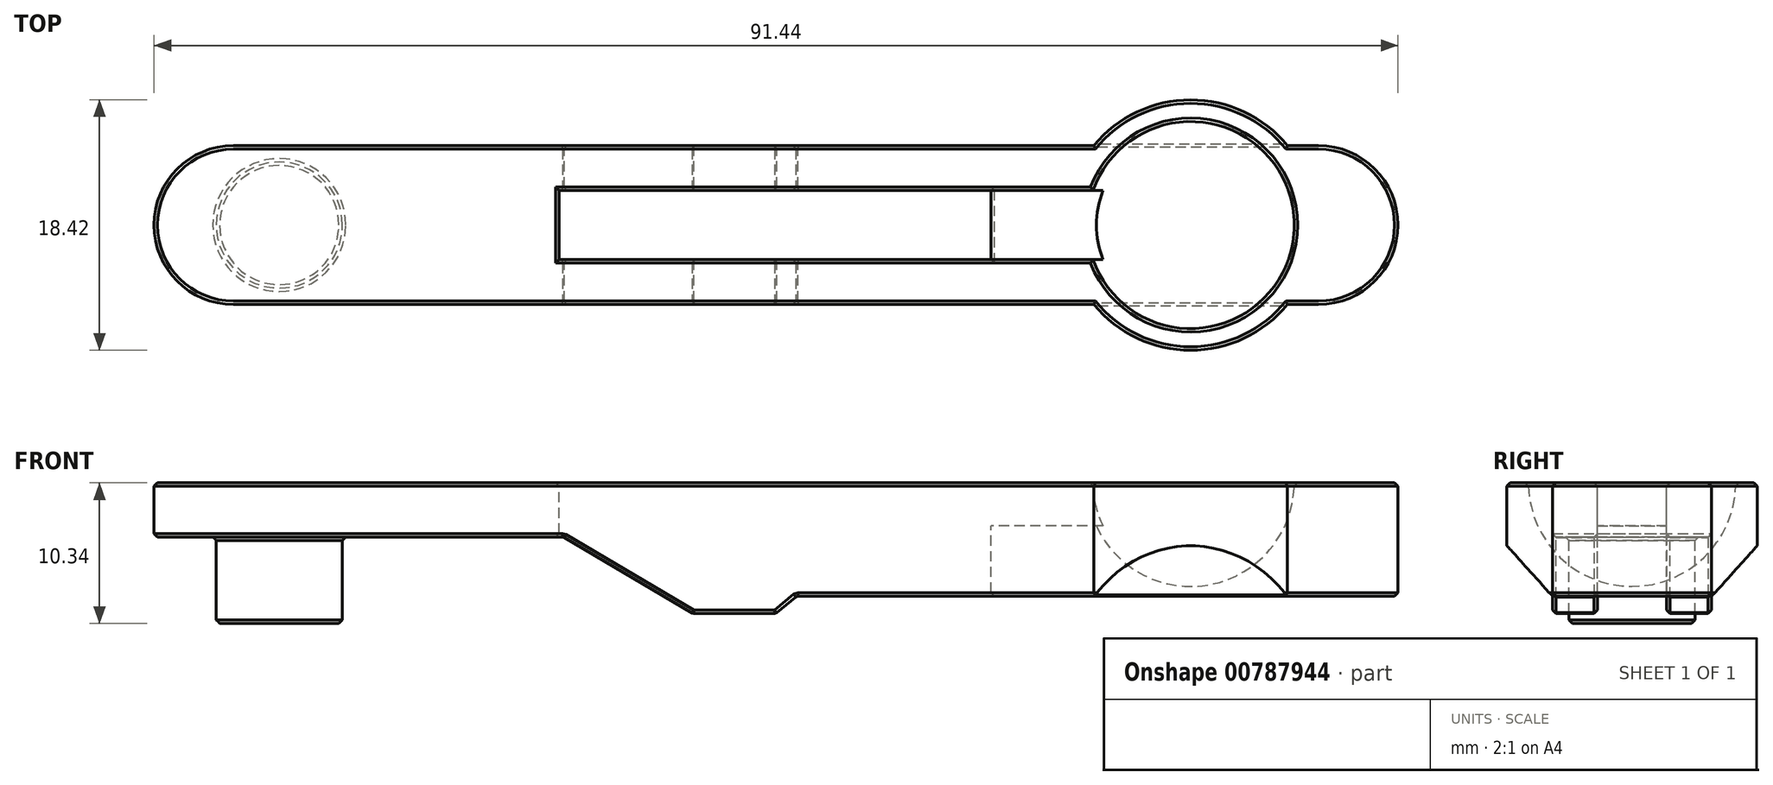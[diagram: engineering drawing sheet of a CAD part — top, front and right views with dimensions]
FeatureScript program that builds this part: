
annotation { "Feature Type Name" : "Feature", "Feature Type Description" : "" }
export const myFeature = defineFeature(function(context is Context, id is Id, definition is map)
    precondition{}
    {
        {
            var Q0;
            Q0=qCreatedBy(makeId("Top.planeOp"),FACE);
            var sketch = newSketch(context, id + "F0", { "sketchPlane" : qUnion([Q0])});
            skLineSegment(sketch, "E0.bottom", {"start": v(45.72, 5.84) * mm, "end": v(-45.72, 5.84) * mm});
            skLineSegment(sketch, "E0.top", {"start": v(45.72, -5.84) * mm, "end": v(-45.72, -5.84) * mm});
            skLineSegment(sketch, "E0.left", {"start": v(45.72, 5.84) * mm, "end": v(45.72, -5.84) * mm});
            skLineSegment(sketch, "E0.right", {"start": v(-45.72, 5.84) * mm, "end": v(-45.72, -5.84) * mm});
            skPoint(sketch, "E0.middle", {"position": v(0, 0) * mm});
            skSolve(sketch);
        }
        {
            var Q0;
            Q0 = qSketchRegion(id + "F0", true);
            extrude(context, id + "F1", {"entities" : qUnion([Q0]), "depth" : 9.6 * mm, "offsetDistance" : 25.4 * mm});
        }
        {
            var Q0;
            Q0=makeQuery(id+"F1.opExtrude","SWEPT_EDGE",EDGE,{"disambiguationData":[OSD([sQuery(id+"F0.wireOp",EDGE,"E0.top"),sQuery(id+"F0.wireOp",EDGE,"E0.right")])]});
            var Q1;
            Q1=makeQuery(id+"F1.opExtrude","SWEPT_EDGE",EDGE,{"disambiguationData":[OSD([sQuery(id+"F0.wireOp",EDGE,"E0.bottom"),sQuery(id+"F0.wireOp",EDGE,"E0.right")])]});
            var Q2;
            Q2=makeQuery(id+"F1.opExtrude","SWEPT_EDGE",EDGE,{"disambiguationData":[OSD([sQuery(id+"F0.wireOp",EDGE,"E0.top"),sQuery(id+"F0.wireOp",EDGE,"E0.left")])]});
            var Q3;
            Q3=makeQuery(id+"F1.opExtrude","SWEPT_EDGE",EDGE,{"disambiguationData":[OSD([sQuery(id+"F0.wireOp",EDGE,"E0.bottom"),sQuery(id+"F0.wireOp",EDGE,"E0.left")])]});
            fillet(context, id + "F2", {"entities" : qUnion([Q0, Q1, Q2, Q3]), "tangentPropagation" : true, "radius" : 5.84 * mm, "defaultsChanged" : true, "vertexSettings" : [], "allowEdgeOverflow" : false});
        }
        {
            var Q0;
            Q0=makeQuery(id+"F1.opExtrude","CAP_FACE",FACE,{"disambiguationData":[OSD([sQuery(id+"F0.wireOp",EDGE,"E0.bottom"),sQuery(id+"F0.wireOp",EDGE,"E0.top"),sQuery(id+"F0.wireOp",EDGE,"E0.left"),sQuery(id+"F0.wireOp",EDGE,"E0.right")])],"isStart":false});
            var sketch = newSketch(context, id + "F3", { "sketchPlane" : qUnion([Q0])});
            skCircle(sketch, "E1", {"center": v(30.48, 0) * mm, "radius": 9.2 * mm});
            skSolve(sketch);
        }
        {
            var Q0;
            Q0 = qSketchRegion(id + "F3", true);
            var Q1;
            Q1=makeQuery(id+"F1.opExtrude","CAP_FACE",FACE,{"disambiguationData":[OSD([sQuery(id+"F0.wireOp",EDGE,"E0.bottom"),sQuery(id+"F0.wireOp",EDGE,"E0.top"),sQuery(id+"F0.wireOp",EDGE,"E0.left"),sQuery(id+"F0.wireOp",EDGE,"E0.right")])],"isStart":true});
            extrude(context, id + "F4", {"entities" : qUnion([Q0]), "operationType" : NewBodyOperationType.ADD, "endBound" : BoundingType.UP_TO_SURFACE, "oppositeDirection" : true, "depth" : 25.4 * mm, "endBoundEntityFace" : qUnion([Q1]), "offsetDistance" : 25.4 * mm});
        }
        {
            var Q0;
            Q0=makeQuery(id+"F4.boolean.opBoolean","MERGE",FACE,{"derivedFrom":[makeQuery(id+"F1.opExtrude","CAP_FACE",FACE,{"disambiguationData":[OSD([sQuery(id+"F0.wireOp",EDGE,"E0.bottom"),sQuery(id+"F0.wireOp",EDGE,"E0.top"),sQuery(id+"F0.wireOp",EDGE,"E0.left"),sQuery(id+"F0.wireOp",EDGE,"E0.right")])],"isStart":false}),makeQuery(id+"F4.opExtrude","CAP_FACE",FACE,{"disambiguationData":[OSD([sQuery(id+"F3.wireOp",EDGE,"E1")])],"isStart":true})]});
            var sketch = newSketch(context, id + "F5", { "sketchPlane" : qUnion([Q0])});
            skArc(sketch, "E2", {"start": v(38.1, 0) * mm, "mid": v(30.48, 7.62) * mm, "end": v(22.86, 0) * mm});
            skLineSegment(sketch, "E3", {"start": v(22.86, 0) * mm, "end": v(38.1, 0) * mm});
            skLineSegment(sketch, "E4", {"start": v(13.82, 0) * mm, "end": v(42.87, 0) * mm, "construction": true});
            skSolve(sketch);
        }
        {
            var Q0;
            Q0 = qSketchRegion(id + "F5", true);
            var Q1;
            Q1=sQuery(id+"F5.wireOp",EDGE,"E4");
            revolve(context, id + "F6", {"operationType" : NewBodyOperationType.REMOVE, "surfaceOperationType" : NewSurfaceOperationType.NEW, "entities" : qUnion([Q0]), "axis" : qUnion([Q1]), "revolveType" : RevolveType.FULL});
        }
        {
            var Q0;
            Q0=makeQuery(id+"F4.boolean.opBoolean","MERGE",FACE,{"derivedFrom":[makeQuery(id+"F1.opExtrude","CAP_FACE",FACE,{"disambiguationData":[OSD([sQuery(id+"F0.wireOp",EDGE,"E0.bottom"),sQuery(id+"F0.wireOp",EDGE,"E0.top"),sQuery(id+"F0.wireOp",EDGE,"E0.left"),sQuery(id+"F0.wireOp",EDGE,"E0.right")])],"isStart":false}),makeQuery(id+"F4.opExtrude","CAP_FACE",FACE,{"disambiguationData":[OSD([sQuery(id+"F3.wireOp",EDGE,"E1")])],"isStart":true})]});
            var sketch = newSketch(context, id + "F7", { "sketchPlane" : qUnion([Q0])});
            skLineSegment(sketch, "E5.bottom", {"start": v(15.8, 2.54) * mm, "end": v(-15.95, 2.54) * mm});
            skLineSegment(sketch, "E5.top", {"start": v(15.8, -2.54) * mm, "end": v(-15.95, -2.54) * mm});
            skLineSegment(sketch, "E5.left", {"start": v(15.8, 2.54) * mm, "end": v(15.8, -2.54) * mm});
            skLineSegment(sketch, "E5.right", {"start": v(-15.95, 2.54) * mm, "end": v(-15.95, -2.54) * mm});
            skPoint(sketch, "E5.middle", {"position": v(-0.08, 0) * mm});
            skSolve(sketch);
        }
        {
            var Q0;
            Q0 = qSketchRegion(id + "F7", true);
            extrude(context, id + "F8", {"entities" : qUnion([Q0]), "operationType" : NewBodyOperationType.REMOVE, "endBound" : BoundingType.THROUGH_ALL, "oppositeDirection" : true, "depth" : 25.4 * mm, "offsetDistance" : 25.4 * mm});
        }
        {
            var Q0;
            Q0=makeQuery(id+"F4.boolean.opBoolean","MERGE",FACE,{"derivedFrom":[makeQuery(id+"F1.opExtrude","CAP_FACE",FACE,{"disambiguationData":[OSD([sQuery(id+"F0.wireOp",EDGE,"E0.bottom"),sQuery(id+"F0.wireOp",EDGE,"E0.top"),sQuery(id+"F0.wireOp",EDGE,"E0.left"),sQuery(id+"F0.wireOp",EDGE,"E0.right")])],"isStart":false}),makeQuery(id+"F4.opExtrude","CAP_FACE",FACE,{"disambiguationData":[OSD([sQuery(id+"F3.wireOp",EDGE,"E1")])],"isStart":true})]});
            var sketch = newSketch(context, id + "F9", { "sketchPlane" : qUnion([Q0])});
            skLineSegment(sketch, "E6.bottom", {"start": v(12.7, -2.54) * mm, "end": v(25.4, -2.54) * mm});
            skLineSegment(sketch, "E6.top", {"start": v(12.7, 2.54) * mm, "end": v(25.4, 2.54) * mm});
            skLineSegment(sketch, "E6.left", {"start": v(12.7, -2.54) * mm, "end": v(12.7, 2.54) * mm});
            skLineSegment(sketch, "E6.right", {"start": v(25.4, -2.54) * mm, "end": v(25.4, 2.54) * mm});
            skSolve(sketch);
        }
        {
            var Q0;
            Q0 = qSketchRegion(id + "F9", true);
            extrude(context, id + "F10", {"entities" : qUnion([Q0]), "operationType" : NewBodyOperationType.REMOVE, "oppositeDirection" : true, "depth" : 3.17 * mm, "offsetDistance" : 25.4 * mm});
        }
        {
            var Q0;
            Q0=qCreatedBy(makeId("Front.planeOp"),FACE);
            var sketch = newSketch(context, id + "F11", { "sketchPlane" : qUnion([Q0])});
            skLineSegment(sketch, "E7", {"start": v(0, 0) * mm, "end": v(1.52, 1.27) * mm});
            skLineSegment(sketch, "E8", {"start": v(1.52, 1.27) * mm, "end": v(46.53, 1.27) * mm});
            skLineSegment(sketch, "E9", {"start": v(46.53, 1.27) * mm, "end": v(46.53, 0) * mm});
            skLineSegment(sketch, "E10", {"start": v(46.53, 0) * mm, "end": v(0, 0) * mm});
            skLineSegment(sketch, "E11", {"start": v(-6.1, 0) * mm, "end": v(-15.62, 5.61) * mm});
            skLineSegment(sketch, "E12", {"start": v(-15.62, 5.61) * mm, "end": v(-45.72, 5.61) * mm});
            skLineSegment(sketch, "E13", {"start": v(-45.72, 5.61) * mm, "end": v(-45.72, 0) * mm});
            skLineSegment(sketch, "E14", {"start": v(-45.72, 0) * mm, "end": v(-6.1, 0) * mm});
            skSolve(sketch);
        }
        {
            var Q0;
            Q0 = qSketchRegion(id + "F11", true);
            extrude(context, id + "F12", {"entities" : qUnion([Q0]), "operationType" : NewBodyOperationType.REMOVE, "depth" : 19.05 * mm, "offsetDistance" : 25.4 * mm, "hasSecondDirection" : true, "secondDirectionBound" : BoundingType.THROUGH_ALL, "secondDirectionOppositeDirection" : true, "secondDirectionDepth" : 25.4 * mm, "symmetric" : true});
        }
        {
            var Q0;
            Q0=makeQuery(id+"F12.boolean.opBoolean","COPY",FACE,{"derivedFrom":makeQuery(id+"F12.opExtrude","SWEPT_FACE",FACE,{"disambiguationData":[OSD([sQuery(id+"F11.wireOp",EDGE,"E12")])]})});
            var sketch = newSketch(context, id + "F13", { "sketchPlane" : qUnion([Q0])});
            skCircle(sketch, "E15", {"center": v(-36.51, 0) * mm, "radius": 4.64 * mm});
            skSolve(sketch);
        }
        {
            var Q0;
            Q0 = qSketchRegion(id + "F13", true);
            extrude(context, id + "F14", {"entities" : qUnion([Q0]), "operationType" : NewBodyOperationType.ADD, "depth" : 6.35 * mm, "offsetDistance" : 25.4 * mm});
        }
        {
            var Q0;
            Q0=qCreatedBy(makeId("Right.planeOp"),FACE);
            var sketch = newSketch(context, id + "F15", { "sketchPlane" : qUnion([Q0])});
            skLineSegment(sketch, "E16", {"start": v(5.84, 1.24) * mm, "end": v(9.27, 5.05) * mm});
            skLineSegment(sketch, "E17", {"start": v(9.27, 5.05) * mm, "end": v(9.27, 1.24) * mm});
            skLineSegment(sketch, "E18", {"start": v(9.27, 1.24) * mm, "end": v(5.84, 1.24) * mm});
            skLineSegment(sketch, "E19.MirrorCS", {"start": v(-9.27, 1.24) * mm, "end": v(-5.84, 1.24) * mm});
            skLineSegment(sketch, "E20.MirrorCS", {"start": v(-9.27, 5.05) * mm, "end": v(-9.27, 1.24) * mm});
            skLineSegment(sketch, "E21.MirrorCS", {"start": v(-5.84, 1.24) * mm, "end": v(-9.27, 5.05) * mm});
            skSolve(sketch);
        }
        {
            var Q0;
            Q0 = qSketchRegion(id + "F15", true);
            extrude(context, id + "F16", {"entities" : qUnion([Q0]), "operationType" : NewBodyOperationType.REMOVE, "endBound" : BoundingType.THROUGH_ALL, "depth" : 25.4 * mm, "offsetDistance" : 25.4 * mm});
        }
        {
            var Q0;
            Q0=makeQuery(id+"F4.boolean.opBoolean","MERGE",FACE,{"derivedFrom":[makeQuery(id+"F1.opExtrude","CAP_FACE",FACE,{"disambiguationData":[OSD([sQuery(id+"F0.wireOp",EDGE,"E0.bottom"),sQuery(id+"F0.wireOp",EDGE,"E0.top"),sQuery(id+"F0.wireOp",EDGE,"E0.left"),sQuery(id+"F0.wireOp",EDGE,"E0.right")])],"isStart":false}),makeQuery(id+"F4.opExtrude","CAP_FACE",FACE,{"disambiguationData":[OSD([sQuery(id+"F3.wireOp",EDGE,"E1")])],"isStart":true})]});
            var Q1;
            Q1=makeQuery(id+"F12.boolean.opBoolean","COPY",FACE,{"derivedFrom":makeQuery(id+"F12.opExtrude","SWEPT_FACE",FACE,{"disambiguationData":[OSD([sQuery(id+"F11.wireOp",EDGE,"E12")])]})});
            var Q2;
            Q2=makeQuery(id+"F14.opExtrude","CAP_FACE",FACE,{"disambiguationData":[OSD([sQuery(id+"F13.wireOp",EDGE,"E15")])],"isStart":false});
            var Q3;
            {var subQ0=sQuery(id+"F0.wireOp",EDGE,"E0.bottom");Q3=makeQuery(id+"F12.boolean.opBoolean","COPY",FACE,{"disambiguationData":[TD([makeQuery(id+"F1.opExtrude","SWEPT_FACE",FACE,{"disambiguationData":[OSD([subQ0])]})])],"derivedFrom":makeQuery(id+"F12.opExtrude","SWEPT_FACE",FACE,{"disambiguationData":[OSD([sQuery(id+"F11.wireOp",EDGE,"E11")])]})});}
            var Q4;
            {var subQ0=sQuery(id+"F0.wireOp",EDGE,"E0.top");Q4=makeQuery(id+"F12.boolean.opBoolean","COPY",FACE,{"disambiguationData":[TD([makeQuery(id+"F1.opExtrude","SWEPT_FACE",FACE,{"disambiguationData":[OSD([subQ0])]})])],"derivedFrom":makeQuery(id+"F12.opExtrude","SWEPT_FACE",FACE,{"disambiguationData":[OSD([sQuery(id+"F11.wireOp",EDGE,"E11")])]})});}
            var Q5;
            {var subQ0=sQuery(id+"F0.wireOp",EDGE,"E0.top");Q5=makeQuery(id+"F12.boolean.opBoolean","SPLIT",FACE,{"disambiguationData":[TD([makeQuery(id+"F1.opExtrude","SWEPT_FACE",FACE,{"disambiguationData":[OSD([subQ0])]})])],"derivedFrom":makeQuery(id+"F4.boolean.opBoolean","MERGE",FACE,{"derivedFrom":[makeQuery(id+"F1.opExtrude","CAP_FACE",FACE,{"disambiguationData":[OSD([sQuery(id+"F0.wireOp",EDGE,"E0.bottom"),subQ0,sQuery(id+"F0.wireOp",EDGE,"E0.left"),sQuery(id+"F0.wireOp",EDGE,"E0.right")])],"isStart":true}),makeQuery(id+"F4.opExtrude","CAP_FACE",FACE,{"disambiguationData":[OSD([sQuery(id+"F3.wireOp",EDGE,"E1")])],"isStart":false})]})});}
            var Q6;
            {var subQ0=sQuery(id+"F0.wireOp",EDGE,"E0.bottom");Q6=makeQuery(id+"F12.boolean.opBoolean","SPLIT",FACE,{"disambiguationData":[TD([makeQuery(id+"F1.opExtrude","SWEPT_FACE",FACE,{"disambiguationData":[OSD([subQ0])]})])],"derivedFrom":makeQuery(id+"F4.boolean.opBoolean","MERGE",FACE,{"derivedFrom":[makeQuery(id+"F1.opExtrude","CAP_FACE",FACE,{"disambiguationData":[OSD([subQ0,sQuery(id+"F0.wireOp",EDGE,"E0.top"),sQuery(id+"F0.wireOp",EDGE,"E0.left"),sQuery(id+"F0.wireOp",EDGE,"E0.right")])],"isStart":true}),makeQuery(id+"F4.opExtrude","CAP_FACE",FACE,{"disambiguationData":[OSD([sQuery(id+"F3.wireOp",EDGE,"E1")])],"isStart":false})]})});}
            var Q7;
            {var subQ0=sQuery(id+"F11.wireOp",EDGE,"E8");var subQ1=sQuery(id+"F11.wireOp",EDGE,"E7");Q7=makeQuery(id+"F12.boolean.opBoolean","COPY",EDGE,{"disambiguationData":[TD([makeQuery(id+"F1.opExtrude","SWEPT_FACE",FACE,{"disambiguationData":[OSD([sQuery(id+"F0.wireOp",EDGE,"E0.bottom")])]})])],"derivedFrom":makeQuery(id+"F12.opExtrude","SWEPT_EDGE",EDGE,{"disambiguationData":[OSD([subQ1,subQ0])]})});}
            var Q8;
            {var subQ0=sQuery(id+"F0.wireOp",EDGE,"E0.top");Q8=makeQuery(id+"F12.boolean.opBoolean","COPY",FACE,{"disambiguationData":[TD([makeQuery(id+"F1.opExtrude","SWEPT_FACE",FACE,{"disambiguationData":[OSD([subQ0])]})])],"derivedFrom":makeQuery(id+"F12.opExtrude","SWEPT_FACE",FACE,{"disambiguationData":[OSD([sQuery(id+"F11.wireOp",EDGE,"E7")])]})});}
            var Q9;
            Q9=makeQuery(id+"F12.boolean.opBoolean","COPY",FACE,{"derivedFrom":makeQuery(id+"F12.opExtrude","SWEPT_FACE",FACE,{"disambiguationData":[OSD([sQuery(id+"F11.wireOp",EDGE,"E8")])]})});
            chamfer(context, id + "F17", {"entities" : qUnion([Q0, Q1, Q2, Q3, Q4, Q5, Q6, Q7, Q8, Q9]), "width" : 0.25 * mm, "tangentPropagation" : true});
        }
    });
